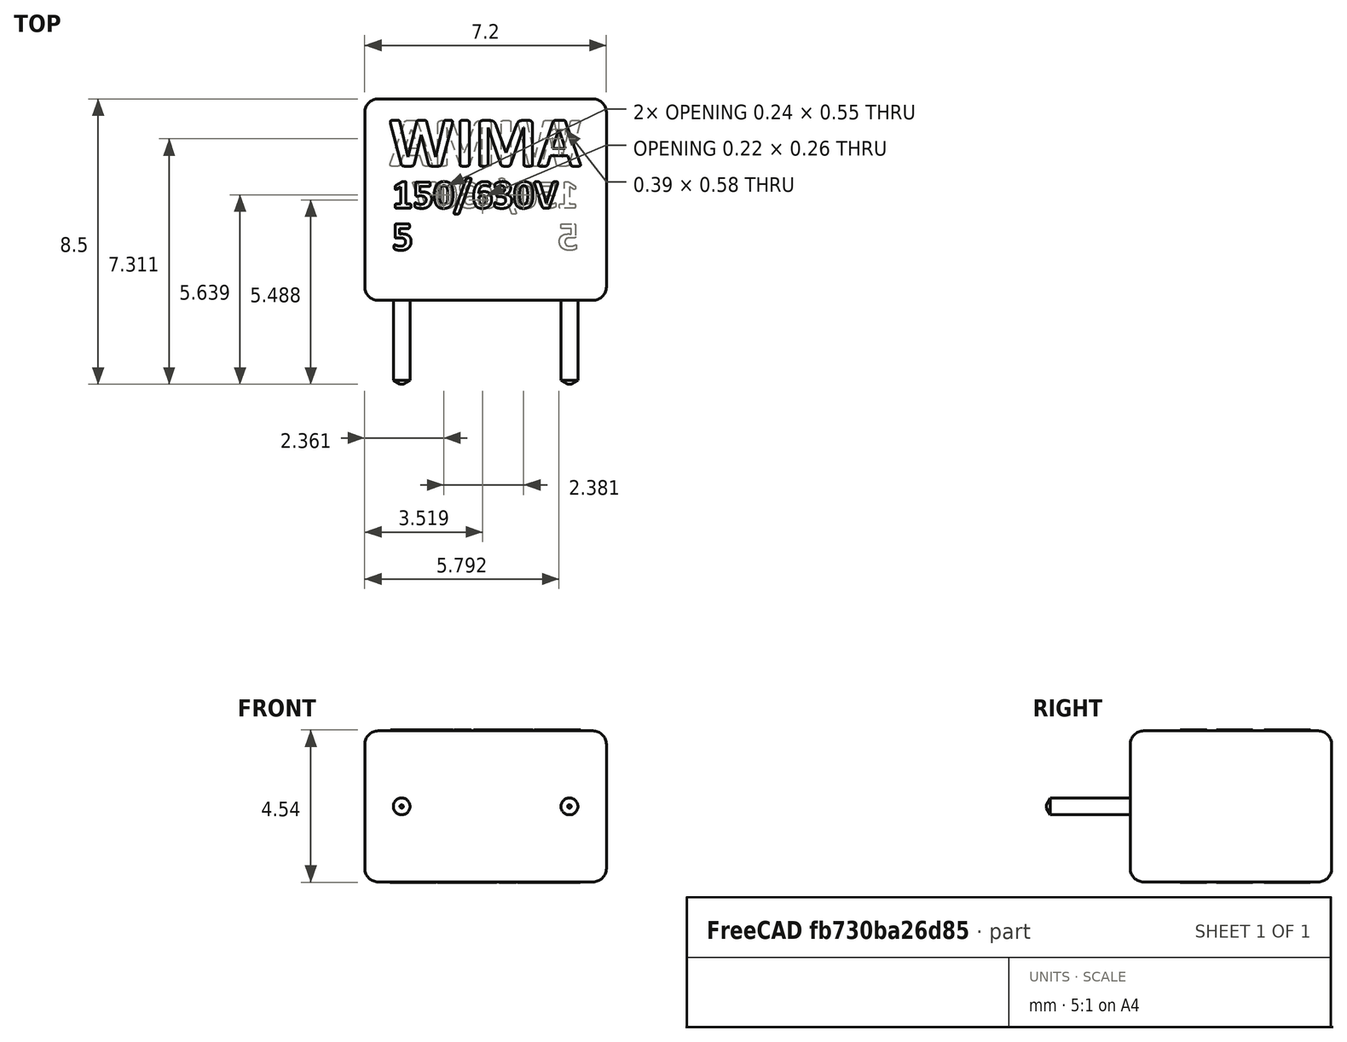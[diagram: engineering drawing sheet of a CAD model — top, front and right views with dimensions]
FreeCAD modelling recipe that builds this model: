
FCSTD DOCUMENT  (FreeCAD 0.17R13528 (Git))
Label: WIMA_D_Case_Extruded_Union
License: All rights reserved
LicenseURL: http://en.wikipedia.org/wiki/All_rights_reserved
objects: Part::Part2DObjectPython×6, Part::Extrusion×6, Part::Feature×1, Part::MultiFuse×1
note: 14 computed .brp shape members not serialized (recipe doc carries the construction recipe); baked Part::Feature solids carry a one-line shape summary decoded from their .brp

FEATURE [Part::Feature] Part__Feature  label="WIMA_D_Case"
  shape: bbox 7.2 x 8.5 x 4.5 mm, 36 faces (baked)
FEATURE [Part::Part2DObjectPython] ShapeString  label="F_WIMA"  # Draft 2D object (typed FeaturePython)
  FontFile = <userpath>/Desktop/Freecad Projects/calibrib.ttf
  Placement = pos=(-0.75,4,2.26) rot=(0,0,1;0rad)
  Size = 1.75
  String = WIMA
  Support = -> [Part__Feature]
  Tracking = 0
FEATURE [Part::Part2DObjectPython] ShapeString001  label="F_Vaule/Rating"  # Draft 2D object (typed FeaturePython)
  FontFile = <userpath>/Desktop/Freecad Projects/calibrib.ttf
  Placement = pos=(-0.65,2.75,2.26) rot=(0,0,1;0rad)
  Size = 1
  String = 150/630V
  Support = -> [Part__Feature]
  Tracking = 0
FEATURE [Part::Part2DObjectPython] ShapeString002  label="F_Tolerance"  # Draft 2D object (typed FeaturePython)
  FontFile = <userpath>/Desktop/Freecad Projects/calibrib.ttf
  Placement = pos=(-0.65,1.5,2.26) rot=(0,0,1;0rad)
  Size = 1
  String = 5
  Support = -> [Part__Feature]
  Tracking = 0
FEATURE [Part::Part2DObjectPython] ShapeString003  label="B_WIMA"  # Draft 2D object (typed FeaturePython)
  FontFile = <userpath>/Desktop/Freecad Projects/calibrib.ttf
  Placement = pos=(5,4,-2.26) rot=(0,1,0;3.14159rad)
  Size = 1.75
  String = WIMA
  Support = -> [Part__Feature]
  Tracking = 0
FEATURE [Part::Part2DObjectPython] ShapeString004  label="B_Value/Rating"  # Draft 2D object (typed FeaturePython)
  FontFile = <userpath>/Desktop/Freecad Projects/calibrib.ttf
  Placement = pos=(4.9,2.75,-2.26) rot=(0,1,0;3.14159rad)
  Size = 1
  String = 150/630V
  Support = -> [Part__Feature]
  Tracking = 0
FEATURE [Part::Part2DObjectPython] ShapeString005  label="B_Tolerance"  # Draft 2D object (typed FeaturePython)
  FontFile = <userpath>/Desktop/Freecad Projects/calibrib.ttf
  Placement = pos=(4.9,1.5,-2.26) rot=(0,1,0;3.14159rad)
  Size = 1
  String = 5
  Support = -> [Part__Feature]
  Tracking = 0
FEATURE [Part::Extrusion] Extrude
  Base = -> ShapeString
  Dir = (0,0,1)
  DirMode = 2
  FaceMakerClass = Part::FaceMakerBullseye
  LengthFwd = 0.02
  LengthRev = 0
  Solid = true
  Symmetric = false
FEATURE [Part::Extrusion] Extrude001
  Base = -> ShapeString001
  Dir = (0,0,1)
  DirMode = 2
  FaceMakerClass = Part::FaceMakerBullseye
  LengthFwd = 0.02
  LengthRev = 0
  Solid = true
  Symmetric = false
FEATURE [Part::Extrusion] Extrude002
  Base = -> ShapeString002
  Dir = (0,0,1)
  DirMode = 2
  FaceMakerClass = Part::FaceMakerBullseye
  LengthFwd = 0.02
  LengthRev = 0
  Solid = true
  Symmetric = false
FEATURE [Part::Extrusion] Extrude003
  Base = -> ShapeString003
  Dir = (0,0,-1)
  DirMode = 2
  FaceMakerClass = Part::FaceMakerBullseye
  LengthFwd = -0.02
  LengthRev = 0
  Solid = true
  Symmetric = false
FEATURE [Part::Extrusion] Extrude004
  Base = -> ShapeString004
  Dir = (0,0,-1)
  DirMode = 2
  FaceMakerClass = Part::FaceMakerBullseye
  LengthFwd = -0.02
  LengthRev = 0
  Solid = true
  Symmetric = false
FEATURE [Part::Extrusion] Extrude005
  Base = -> ShapeString005
  Dir = (0,0,-1)
  DirMode = 2
  FaceMakerClass = Part::FaceMakerBullseye
  LengthFwd = -0.02
  LengthRev = 0
  Solid = true
  Symmetric = false
FEATURE [Part::MultiFuse] Fusion
  Shapes = -> [Part__Feature,Extrude001,Extrude004,Extrude,Extrude003,Extrude005,Extrude002]
